# Revit family: slc-4712
name_source: partatom
category: Pipe Accessories
units: mm (PartAtom-declared; Revit-internal decimal feet)

## family parameters
Cut with Voids When Loaded = No
Host = Face
OmniClass Number = 23.65.55.00
OmniClass Title = Distribution of Supplied Liquids/Gases
Part Type = Normal
Round Connector Dimension = Use Radius
Shared = No

## types (2) — shared parameters
Date Modified = January 30, 2015
Description = Not Available
Equipment Abbreviation = SH
Family Version = 1.0
Gallons Per Minute = 0.500 GPM
Manufacturer = Symmons Industries, Inc.
Model = Not Available
Model Disclaimer = Contact Symmons Industries, Inc. For More Information
Product Page URL = http://www.symmons.com
URL = http://www.symmons.com
z GPM GPM = 0.000 GPM
zero-valued in all types: Default Elevation, z GPM Number, z Type Finish, z Type Flow Restrictor, z Type GPM

## per-type parameters (varying)
| type | Product Material |
| Polished Chrome | Chrome - Symmons - Polished |
| Satin Nickel | Nickel - Symmons - Satin |

## geometry (parser evidence)
native form markers: Sweep x2
no freeform markers — native parametric forms only
